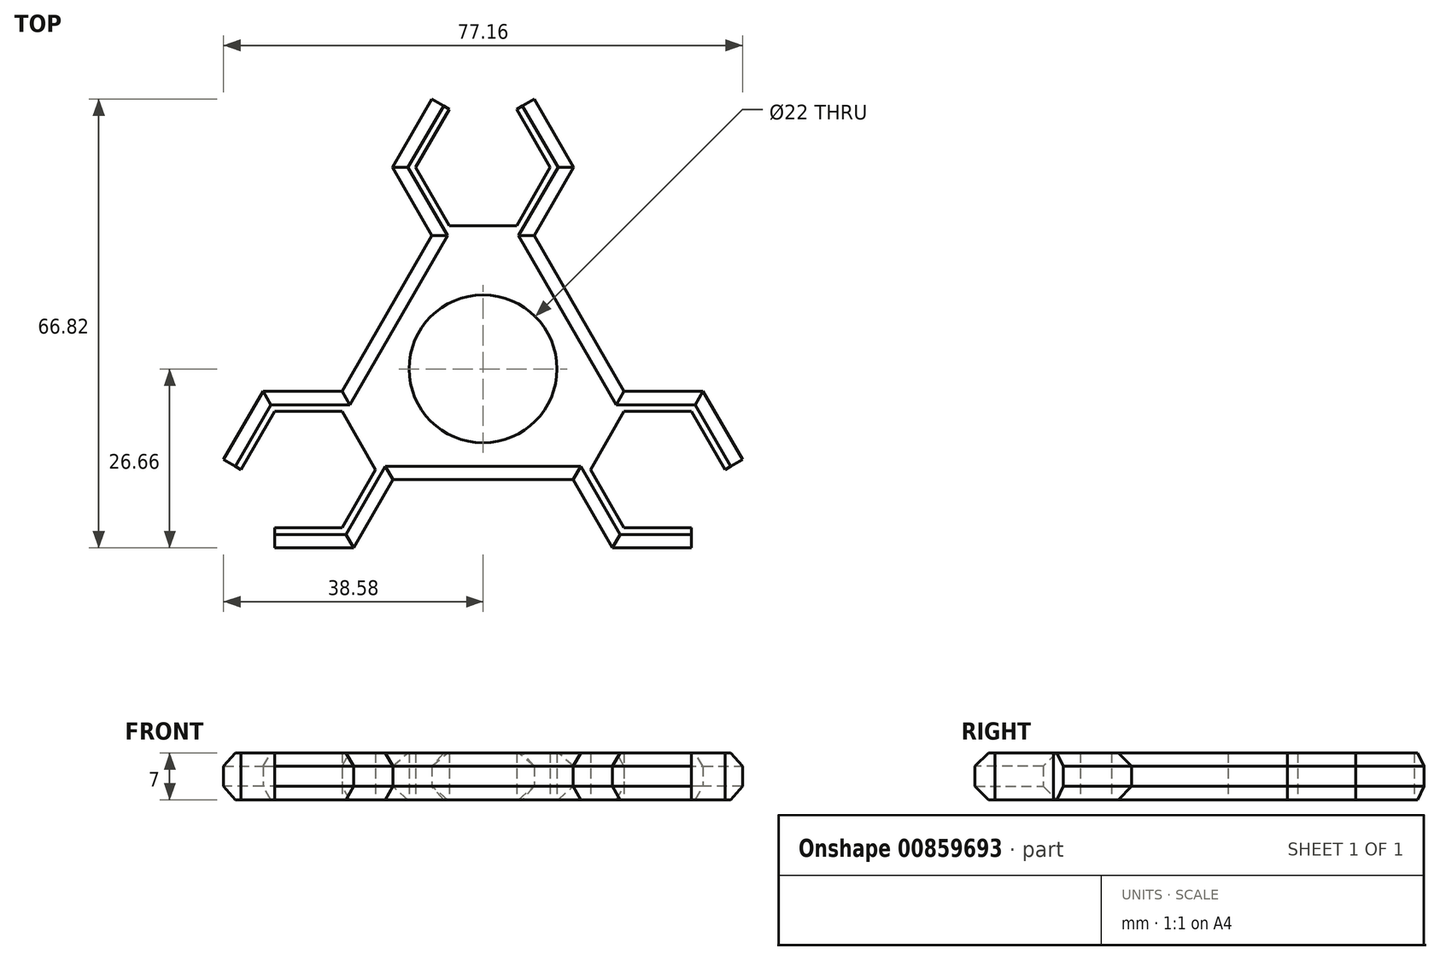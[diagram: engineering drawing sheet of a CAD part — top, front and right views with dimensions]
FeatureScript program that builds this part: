
annotation { "Feature Type Name" : "Feature", "Feature Type Description" : "" }
export const myFeature = defineFeature(function(context is Context, id is Id, definition is map)
    precondition{}
    {
        {
            var Q0;
            Q0=qCreatedBy(makeId("Top.planeOp"),FACE);
            var sketch = newSketch(context, id + "F0", { "sketchPlane" : qUnion([Q0])});
            skCircle(sketch, "E0", {"center": v(0, 0) * mm, "radius": 11 * mm});
            skCircle(sketch, "E1.cCircle", {"center": v(0, 30) * mm, "radius": 8.66 * mm, "construction": true});
            skLineSegment(sketch, "E1.0", {"start": v(5, 21.34) * mm, "end": v(-5, 21.34) * mm});
            skLineSegment(sketch, "E1.1", {"start": v(-5, 21.34) * mm, "end": v(-10, 30) * mm});
            skLineSegment(sketch, "E1.2", {"start": v(-10, 30) * mm, "end": v(-5, 38.66) * mm});
            skLineSegment(sketch, "E1.3", {"start": v(-5, 38.66) * mm, "end": v(5, 38.66) * mm});
            skLineSegment(sketch, "E1.4", {"start": v(5, 38.66) * mm, "end": v(10, 30) * mm});
            skLineSegment(sketch, "E1.5", {"start": v(10, 30) * mm, "end": v(5, 21.34) * mm});
            skPoint(sketch, "E1.0.midPoint", {"position": v(0, 21.34) * mm});
            skCircle(sketch, "E2.cCircle", {"center": v(-25.98, -15) * mm, "radius": 8.66 * mm, "construction": true});
            skLineSegment(sketch, "E2.0", {"start": v(-15.98, -15) * mm, "end": v(-20.98, -23.66) * mm});
            skLineSegment(sketch, "E2.1", {"start": v(-20.98, -23.66) * mm, "end": v(-30.98, -23.66) * mm});
            skLineSegment(sketch, "E2.2", {"start": v(-30.98, -23.66) * mm, "end": v(-35.98, -15) * mm});
            skLineSegment(sketch, "E2.3", {"start": v(-35.98, -15) * mm, "end": v(-30.98, -6.34) * mm});
            skLineSegment(sketch, "E2.4", {"start": v(-30.98, -6.34) * mm, "end": v(-20.98, -6.34) * mm});
            skLineSegment(sketch, "E2.5", {"start": v(-20.98, -6.34) * mm, "end": v(-15.98, -15) * mm});
            skPoint(sketch, "E2.0.midPoint", {"position": v(-18.48, -19.33) * mm});
            skCircle(sketch, "E3.cCircle", {"center": v(25.98, -15) * mm, "radius": 8.66 * mm, "construction": true});
            skLineSegment(sketch, "E3.0", {"start": v(35.98, -15) * mm, "end": v(30.98, -23.66) * mm});
            skLineSegment(sketch, "E3.1", {"start": v(30.98, -23.66) * mm, "end": v(20.98, -23.66) * mm});
            skLineSegment(sketch, "E3.2", {"start": v(20.98, -23.66) * mm, "end": v(15.98, -15) * mm});
            skLineSegment(sketch, "E3.3", {"start": v(15.98, -15) * mm, "end": v(20.98, -6.34) * mm});
            skLineSegment(sketch, "E3.4", {"start": v(20.98, -6.34) * mm, "end": v(30.98, -6.34) * mm});
            skLineSegment(sketch, "E3.5", {"start": v(30.98, -6.34) * mm, "end": v(35.98, -15) * mm});
            skPoint(sketch, "E3.0.midPoint", {"position": v(33.48, -19.33) * mm});
            skLineSegment(sketch, "E4.0", {"start": v(-38.58, -13.5) * mm, "end": v(-33.58, -4.84) * mm});
            skLineSegment(sketch, "E5.0", {"start": v(-20.98, -26.66) * mm, "end": v(-30.98, -26.66) * mm});
            skLineSegment(sketch, "E6.0", {"start": v(-13.38, -16.5) * mm, "end": v(-18.38, -25.16) * mm});
            skLineSegment(sketch, "E7.0", {"start": v(-30.98, -3.34) * mm, "end": v(-20.98, -3.34) * mm});
            skLineSegment(sketch, "E8.0", {"start": v(30.98, -26.66) * mm, "end": v(20.98, -26.66) * mm});
            skLineSegment(sketch, "E9.0", {"start": v(18.38, -25.16) * mm, "end": v(13.38, -16.5) * mm});
            skLineSegment(sketch, "E10.0", {"start": v(33.58, -4.84) * mm, "end": v(38.58, -13.5) * mm});
            skLineSegment(sketch, "E11.0", {"start": v(20.98, -3.34) * mm, "end": v(30.98, -3.34) * mm});
            skLineSegment(sketch, "E12.0", {"start": v(-12.6, 31.5) * mm, "end": v(-7.6, 40.16) * mm});
            skLineSegment(sketch, "E13.0", {"start": v(-7.6, 19.84) * mm, "end": v(-12.6, 28.5) * mm});
            skLineSegment(sketch, "E14.0", {"start": v(7.6, 40.16) * mm, "end": v(12.6, 31.5) * mm});
            skLineSegment(sketch, "E15.0", {"start": v(12.6, 28.5) * mm, "end": v(7.6, 19.84) * mm});
            skLineSegment(sketch, "E16", {"start": v(-20.98, -3.34) * mm, "end": v(-7.6, 19.84) * mm});
            skLineSegment(sketch, "E17", {"start": v(7.6, 19.84) * mm, "end": v(20.98, -3.34) * mm});
            skLineSegment(sketch, "E18", {"start": v(-13.38, -16.5) * mm, "end": v(13.38, -16.5) * mm});
            skLineSegment(sketch, "E19", {"start": v(30.98, -3.34) * mm, "end": v(32.71, -3.34) * mm});
            skLineSegment(sketch, "E20", {"start": v(-30.98, -3.34) * mm, "end": v(-32.71, -3.34) * mm});
            skLineSegment(sketch, "E21", {"start": v(20.98, -26.66) * mm, "end": v(19.25, -26.66) * mm});
            skLineSegment(sketch, "E22", {"start": v(-20.98, -26.66) * mm, "end": v(-19.25, -26.66) * mm});
            skLineSegment(sketch, "E23", {"start": v(-12.6, 28.5) * mm, "end": v(-13.46, 30) * mm});
            skLineSegment(sketch, "E24", {"start": v(12.6, 28.5) * mm, "end": v(13.46, 30) * mm});
            skLineSegment(sketch, "E25", {"start": v(-12.6, 31.5) * mm, "end": v(-13.46, 30) * mm});
            skLineSegment(sketch, "E26", {"start": v(12.6, 31.5) * mm, "end": v(13.46, 30) * mm});
            skLineSegment(sketch, "E27", {"start": v(-33.58, -4.84) * mm, "end": v(-32.71, -3.34) * mm});
            skLineSegment(sketch, "E28", {"start": v(-18.38, -25.16) * mm, "end": v(-19.25, -26.66) * mm});
            skLineSegment(sketch, "E29", {"start": v(33.58, -4.84) * mm, "end": v(32.71, -3.34) * mm});
            skLineSegment(sketch, "E30", {"start": v(18.38, -25.16) * mm, "end": v(19.25, -26.66) * mm});
            skPoint(sketch, "E31.orphan", {"position": v(5.2, -26.66) * mm});
            skLineSegment(sketch, "E32", {"start": v(-38.58, -13.5) * mm, "end": v(-35.98, -15) * mm});
            skLineSegment(sketch, "E33", {"start": v(-30.98, -26.66) * mm, "end": v(-30.98, -23.66) * mm});
            skLineSegment(sketch, "E34", {"start": v(-7.6, 40.16) * mm, "end": v(-5, 38.66) * mm});
            skLineSegment(sketch, "E35", {"start": v(7.6, 40.16) * mm, "end": v(5, 38.66) * mm});
            skLineSegment(sketch, "E36", {"start": v(35.98, -15) * mm, "end": v(38.58, -13.5) * mm});
            skLineSegment(sketch, "E37", {"start": v(30.98, -26.66) * mm, "end": v(30.98, -23.66) * mm});
            skSolve(sketch);
        }
        {
            var Q0;
            Q0=makeQuery(id+"F0.imprint","IMPRINT",FACE,{"disambiguationData":[TD([[makeQuery(id+"F0.imprint","IMPRINT",EDGE,{"derivedFrom":sQuery(id+"F0.wireOp",EDGE,"E0")}),-1.0]])]});
            extrude(context, id + "F1", {"entities" : qUnion([Q0]), "depth" : 7 * mm, "offsetDistance" : 25 * mm});
        }
        {
            var Q0;
            Q0=makeQuery(id+"F1.opExtrude","CAP_EDGE",EDGE,{"disambiguationData":[OSD([sQuery(id+"F0.wireOp",EDGE,"E10.0"),sQuery(id+"F0.wireOp",EDGE,"E29")])],"isStart":false});
            var Q1;
            Q1=makeQuery(id+"F1.opExtrude","CAP_EDGE",EDGE,{"disambiguationData":[OSD([sQuery(id+"F0.wireOp",EDGE,"E11.0"),sQuery(id+"F0.wireOp",EDGE,"E19")])],"isStart":false});
            var Q2;
            Q2=makeQuery(id+"F1.opExtrude","CAP_EDGE",EDGE,{"disambiguationData":[OSD([sQuery(id+"F0.wireOp",EDGE,"E10.0"),sQuery(id+"F0.wireOp",EDGE,"E29")])],"isStart":true});
            var Q3;
            Q3=makeQuery(id+"F1.opExtrude","CAP_EDGE",EDGE,{"disambiguationData":[OSD([sQuery(id+"F0.wireOp",EDGE,"E11.0"),sQuery(id+"F0.wireOp",EDGE,"E19")])],"isStart":true});
            var Q4;
            Q4=makeQuery(id+"F1.opExtrude","CAP_EDGE",EDGE,{"disambiguationData":[OSD([sQuery(id+"F0.wireOp",EDGE,"E17")])],"isStart":true});
            var Q5;
            Q5=makeQuery(id+"F1.opExtrude","CAP_EDGE",EDGE,{"disambiguationData":[OSD([sQuery(id+"F0.wireOp",EDGE,"E17")])],"isStart":false});
            var Q6;
            Q6=makeQuery(id+"F1.opExtrude","CAP_EDGE",EDGE,{"disambiguationData":[OSD([sQuery(id+"F0.wireOp",EDGE,"E15.0"),sQuery(id+"F0.wireOp",EDGE,"E24")])],"isStart":false});
            var Q7;
            Q7=makeQuery(id+"F1.opExtrude","CAP_EDGE",EDGE,{"disambiguationData":[OSD([sQuery(id+"F0.wireOp",EDGE,"E15.0"),sQuery(id+"F0.wireOp",EDGE,"E24")])],"isStart":true});
            var Q8;
            Q8=makeQuery(id+"F1.opExtrude","CAP_EDGE",EDGE,{"disambiguationData":[OSD([sQuery(id+"F0.wireOp",EDGE,"E14.0"),sQuery(id+"F0.wireOp",EDGE,"E26")])],"isStart":true});
            var Q9;
            Q9=makeQuery(id+"F1.opExtrude","CAP_EDGE",EDGE,{"disambiguationData":[OSD([sQuery(id+"F0.wireOp",EDGE,"E14.0"),sQuery(id+"F0.wireOp",EDGE,"E26")])],"isStart":false});
            var Q10;
            Q10=makeQuery(id+"F1.opExtrude","CAP_EDGE",EDGE,{"disambiguationData":[OSD([sQuery(id+"F0.wireOp",EDGE,"E5.0"),sQuery(id+"F0.wireOp",EDGE,"E22")])],"isStart":false});
            var Q11;
            Q11=makeQuery(id+"F1.opExtrude","CAP_EDGE",EDGE,{"disambiguationData":[OSD([sQuery(id+"F0.wireOp",EDGE,"E5.0"),sQuery(id+"F0.wireOp",EDGE,"E22")])],"isStart":true});
            var Q12;
            Q12=makeQuery(id+"F1.opExtrude","CAP_EDGE",EDGE,{"disambiguationData":[OSD([sQuery(id+"F0.wireOp",EDGE,"E6.0"),sQuery(id+"F0.wireOp",EDGE,"E28")])],"isStart":false});
            var Q13;
            Q13=makeQuery(id+"F1.opExtrude","CAP_EDGE",EDGE,{"disambiguationData":[OSD([sQuery(id+"F0.wireOp",EDGE,"E6.0"),sQuery(id+"F0.wireOp",EDGE,"E28")])],"isStart":true});
            var Q14;
            Q14=makeQuery(id+"F1.opExtrude","CAP_EDGE",EDGE,{"disambiguationData":[OSD([sQuery(id+"F0.wireOp",EDGE,"E18")])],"isStart":false});
            var Q15;
            Q15=makeQuery(id+"F1.opExtrude","CAP_EDGE",EDGE,{"disambiguationData":[OSD([sQuery(id+"F0.wireOp",EDGE,"E18")])],"isStart":true});
            var Q16;
            Q16=makeQuery(id+"F1.opExtrude","CAP_EDGE",EDGE,{"disambiguationData":[OSD([sQuery(id+"F0.wireOp",EDGE,"E9.0"),sQuery(id+"F0.wireOp",EDGE,"E30")])],"isStart":false});
            var Q17;
            Q17=makeQuery(id+"F1.opExtrude","CAP_EDGE",EDGE,{"disambiguationData":[OSD([sQuery(id+"F0.wireOp",EDGE,"E9.0"),sQuery(id+"F0.wireOp",EDGE,"E30")])],"isStart":true});
            var Q18;
            Q18=makeQuery(id+"F1.opExtrude","CAP_EDGE",EDGE,{"disambiguationData":[OSD([sQuery(id+"F0.wireOp",EDGE,"E8.0"),sQuery(id+"F0.wireOp",EDGE,"E21")])],"isStart":true});
            var Q19;
            Q19=makeQuery(id+"F1.opExtrude","CAP_EDGE",EDGE,{"disambiguationData":[OSD([sQuery(id+"F0.wireOp",EDGE,"E8.0"),sQuery(id+"F0.wireOp",EDGE,"E21")])],"isStart":false});
            var Q20;
            Q20=makeQuery(id+"F1.opExtrude","CAP_EDGE",EDGE,{"disambiguationData":[OSD([sQuery(id+"F0.wireOp",EDGE,"E12.0"),sQuery(id+"F0.wireOp",EDGE,"E25")])],"isStart":false});
            var Q21;
            Q21=makeQuery(id+"F1.opExtrude","CAP_EDGE",EDGE,{"disambiguationData":[OSD([sQuery(id+"F0.wireOp",EDGE,"E12.0"),sQuery(id+"F0.wireOp",EDGE,"E25")])],"isStart":true});
            var Q22;
            Q22=makeQuery(id+"F1.opExtrude","CAP_EDGE",EDGE,{"disambiguationData":[OSD([sQuery(id+"F0.wireOp",EDGE,"E13.0"),sQuery(id+"F0.wireOp",EDGE,"E23")])],"isStart":false});
            var Q23;
            Q23=makeQuery(id+"F1.opExtrude","CAP_EDGE",EDGE,{"disambiguationData":[OSD([sQuery(id+"F0.wireOp",EDGE,"E13.0"),sQuery(id+"F0.wireOp",EDGE,"E23")])],"isStart":true});
            var Q24;
            Q24=makeQuery(id+"F1.opExtrude","CAP_EDGE",EDGE,{"disambiguationData":[OSD([sQuery(id+"F0.wireOp",EDGE,"E16")])],"isStart":false});
            var Q25;
            Q25=makeQuery(id+"F1.opExtrude","CAP_EDGE",EDGE,{"disambiguationData":[OSD([sQuery(id+"F0.wireOp",EDGE,"E16")])],"isStart":true});
            var Q26;
            Q26=makeQuery(id+"F1.opExtrude","CAP_EDGE",EDGE,{"disambiguationData":[OSD([sQuery(id+"F0.wireOp",EDGE,"E7.0"),sQuery(id+"F0.wireOp",EDGE,"E20")])],"isStart":false});
            var Q27;
            Q27=makeQuery(id+"F1.opExtrude","CAP_EDGE",EDGE,{"disambiguationData":[OSD([sQuery(id+"F0.wireOp",EDGE,"E7.0"),sQuery(id+"F0.wireOp",EDGE,"E20")])],"isStart":true});
            var Q28;
            Q28=makeQuery(id+"F1.opExtrude","CAP_EDGE",EDGE,{"disambiguationData":[OSD([sQuery(id+"F0.wireOp",EDGE,"E4.0"),sQuery(id+"F0.wireOp",EDGE,"E27")])],"isStart":true});
            var Q29;
            Q29=makeQuery(id+"F1.opExtrude","CAP_EDGE",EDGE,{"disambiguationData":[OSD([sQuery(id+"F0.wireOp",EDGE,"E4.0"),sQuery(id+"F0.wireOp",EDGE,"E27")])],"isStart":false});
            chamfer(context, id + "F2", {"entities" : qUnion([Q0, Q1, Q2, Q3, Q4, Q5, Q6, Q7, Q8, Q9, Q10, Q11, Q12, Q13, Q14, Q15, Q16, Q17, Q18, Q19, Q20, Q21, Q22, Q23, Q24, Q25, Q26, Q27, Q28, Q29]), "width" : 2 * mm, "tangentPropagation" : true});
        }
    });
